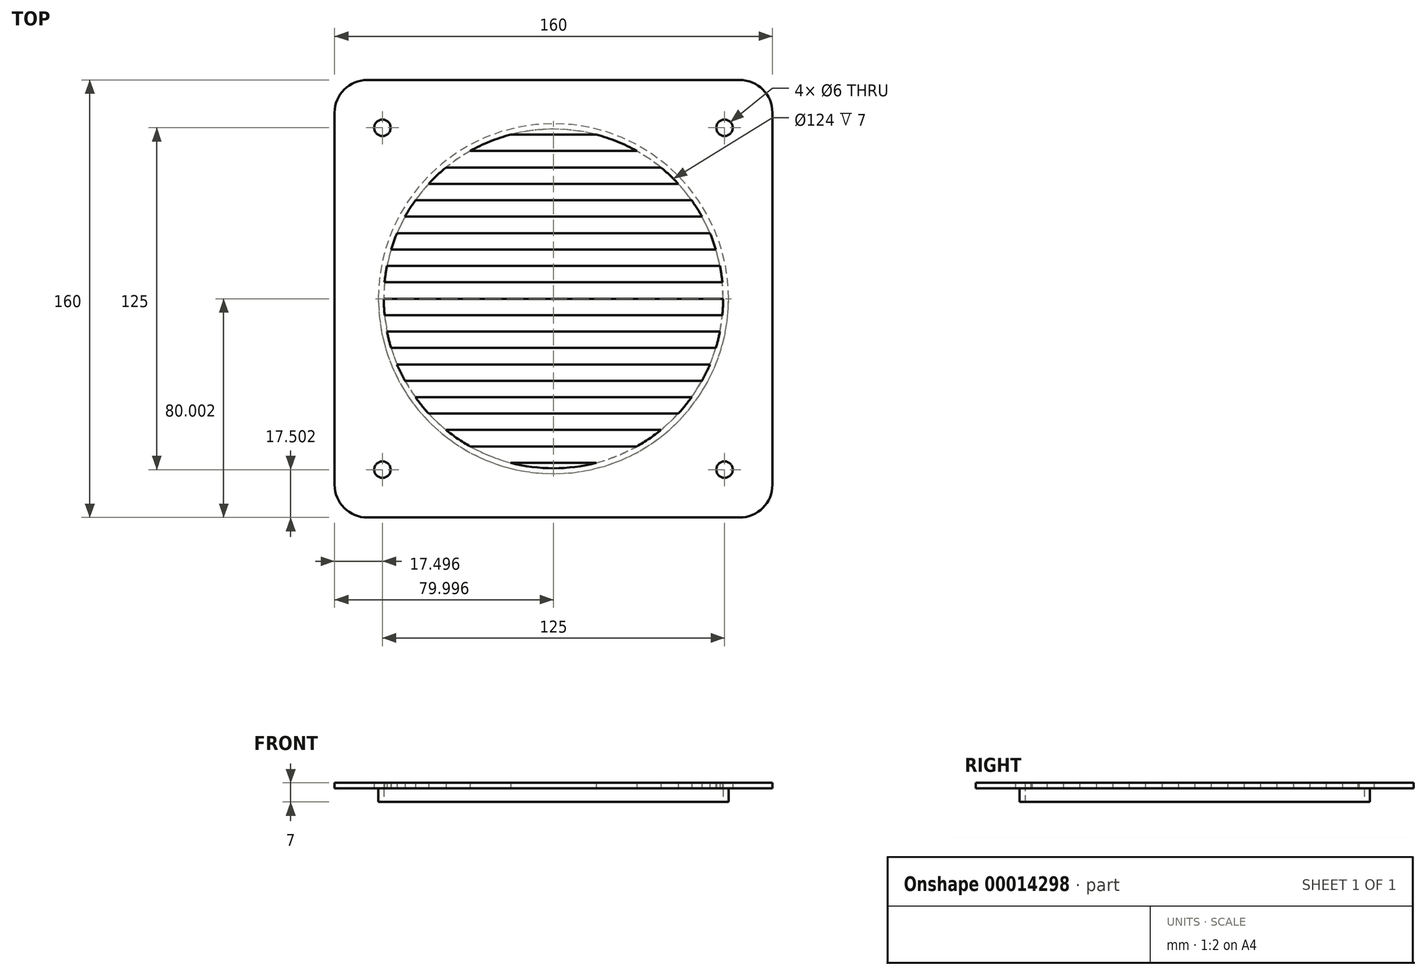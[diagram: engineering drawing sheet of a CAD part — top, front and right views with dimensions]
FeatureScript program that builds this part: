
annotation { "Feature Type Name" : "Feature", "Feature Type Description" : "" }
export const myFeature = defineFeature(function(context is Context, id is Id, definition is map)
    precondition{}
    {
        {
            var Q0;
            Q0=qCreatedBy(makeId("Top.planeOp"),FACE);
            var sketch = newSketch(context, id + "F0", { "sketchPlane" : qUnion([Q0])});
            skLineSegment(sketch, "E0.bottom", {"start": v(-104.32, 77.03) * mm, "end": v(55.68, 77.03) * mm});
            skLineSegment(sketch, "E0.top", {"start": v(-104.32, -82.97) * mm, "end": v(55.68, -82.97) * mm});
            skLineSegment(sketch, "E0.left", {"start": v(-104.32, 77.03) * mm, "end": v(-104.32, -82.97) * mm});
            skLineSegment(sketch, "E0.right", {"start": v(55.68, 77.03) * mm, "end": v(55.68, -82.97) * mm});
            skLineSegment(sketch, "E1", {"start": v(-24.32, 77.03) * mm, "end": v(-24.32, -82.97) * mm, "construction": true});
            skLineSegment(sketch, "E2", {"start": v(-104.32, -2.97) * mm, "end": v(55.68, -2.97) * mm, "construction": true});
            skPoint(sketch, "E3", {"position": v(-24.32, -2.97) * mm});
            skCircle(sketch, "E4", {"center": v(-24.32, -2.97) * mm, "radius": 62 * mm});
            skLineSegment(sketch, "E5", {"start": v(-86.32, -2.97) * mm, "end": v(37.68, -2.97) * mm});
            skLineSegment(sketch, "E6", {"start": v(-86.03, 3.03) * mm, "end": v(37.38, 3.03) * mm});
            skLineSegment(sketch, "E7", {"start": v(-85.15, 9.03) * mm, "end": v(36.5, 9.03) * mm});
            skLineSegment(sketch, "E8", {"start": v(-83.65, 15.03) * mm, "end": v(35, 15.03) * mm});
            skLineSegment(sketch, "E9", {"start": v(-81.5, 21.03) * mm, "end": v(32.84, 21.03) * mm});
            skLineSegment(sketch, "E10", {"start": v(-78.58, 27.03) * mm, "end": v(29.93, 27.03) * mm});
            skLineSegment(sketch, "E11", {"start": v(-74.8, 33.03) * mm, "end": v(26.15, 33.03) * mm});
            skLineSegment(sketch, "E12", {"start": v(-69.93, 39.03) * mm, "end": v(21.28, 39.03) * mm});
            skCircle(sketch, "E13", {"center": v(-86.82, -65.47) * mm, "radius": 3 * mm});
            skLineSegment(sketch, "E14", {"start": v(-86.82, -65.47) * mm, "end": v(-86.82, 59.53) * mm, "construction": true});
            skLineSegment(sketch, "E15", {"start": v(-86.82, 59.53) * mm, "end": v(38.18, 59.53) * mm, "construction": true});
            skLineSegment(sketch, "E16", {"start": v(38.18, 59.53) * mm, "end": v(38.18, -65.47) * mm, "construction": true});
            skLineSegment(sketch, "E17", {"start": v(38.18, -65.47) * mm, "end": v(-86.82, -65.47) * mm, "construction": true});
            skPoint(sketch, "E18", {"position": v(-24.32, 59.53) * mm});
            skPoint(sketch, "E19", {"position": v(38.18, -2.97) * mm});
            skLineSegment(sketch, "E20", {"start": v(-63.57, 45.03) * mm, "end": v(14.92, 45.03) * mm});
            skLineSegment(sketch, "E21", {"start": v(-54.79, 51.03) * mm, "end": v(6.14, 51.03) * mm});
            skLineSegment(sketch, "E22", {"start": v(-39.94, 57.03) * mm, "end": v(-8.7, 57.03) * mm});
            skLineSegment(sketch, "E23.0.MirrorCS", {"start": v(-86.03, -8.97) * mm, "end": v(37.38, -8.97) * mm});
            skLineSegment(sketch, "E23.1.MirrorCS", {"start": v(-85.15, -14.97) * mm, "end": v(36.5, -14.97) * mm});
            skLineSegment(sketch, "E23.2.MirrorCS", {"start": v(-83.65, -20.97) * mm, "end": v(35, -20.97) * mm});
            skLineSegment(sketch, "E23.3.MirrorCS", {"start": v(-81.5, -26.97) * mm, "end": v(32.84, -26.97) * mm});
            skLineSegment(sketch, "E23.4.MirrorCS", {"start": v(-78.58, -32.97) * mm, "end": v(29.93, -32.97) * mm});
            skLineSegment(sketch, "E23.5.MirrorCS", {"start": v(-74.8, -38.97) * mm, "end": v(26.15, -38.97) * mm});
            skLineSegment(sketch, "E23.6.MirrorCS", {"start": v(-69.93, -44.97) * mm, "end": v(21.28, -44.97) * mm});
            skLineSegment(sketch, "E23.7.MirrorCS", {"start": v(-63.57, -50.97) * mm, "end": v(14.92, -50.97) * mm});
            skLineSegment(sketch, "E23.8.MirrorCS", {"start": v(-39.94, -62.97) * mm, "end": v(-8.7, -62.97) * mm});
            skLineSegment(sketch, "E23.9.MirrorCS", {"start": v(-54.79, -56.97) * mm, "end": v(6.14, -56.97) * mm});
            skCircle(sketch, "E24", {"center": v(-86.82, 59.53) * mm, "radius": 3 * mm});
            skCircle(sketch, "E25", {"center": v(38.18, 59.53) * mm, "radius": 3 * mm});
            skCircle(sketch, "E26", {"center": v(38.18, -65.47) * mm, "radius": 3 * mm});
            skSolve(sketch);
        }
        {
            var Q0;
            {var subQ0=sQuery(id+"F0.wireOp",EDGE,"E22");Q0=makeQuery(id+"F0.imprint","IMPRINT",FACE,{"disambiguationData":[TD([[makeQuery(id+"F0.imprint","IMPRINT",EDGE,{"derivedFrom":subQ0}),1.0]])]});}
            var Q1;
            {var subQ1=sQuery(id+"F0.wireOp",EDGE,"E20");Q1=makeQuery(id+"F0.imprint","IMPRINT",FACE,{"disambiguationData":[TD([[makeQuery(id+"F0.imprint","IMPRINT",EDGE,{"derivedFrom":subQ1}),1.0]])]});}
            var Q2;
            {var subQ1=sQuery(id+"F0.wireOp",EDGE,"E11");Q2=makeQuery(id+"F0.imprint","IMPRINT",FACE,{"disambiguationData":[TD([[makeQuery(id+"F0.imprint","IMPRINT",EDGE,{"derivedFrom":subQ1}),1.0]])]});}
            var Q3;
            {var subQ1=sQuery(id+"F0.wireOp",EDGE,"E9");Q3=makeQuery(id+"F0.imprint","IMPRINT",FACE,{"disambiguationData":[TD([[makeQuery(id+"F0.imprint","IMPRINT",EDGE,{"derivedFrom":subQ1}),1.0]])]});}
            var Q4;
            {var subQ1=sQuery(id+"F0.wireOp",EDGE,"E7");Q4=makeQuery(id+"F0.imprint","IMPRINT",FACE,{"disambiguationData":[TD([[makeQuery(id+"F0.imprint","IMPRINT",EDGE,{"derivedFrom":subQ1}),1.0]])]});}
            var Q5;
            {var subQ1=sQuery(id+"F0.wireOp",EDGE,"E5");Q5=makeQuery(id+"F0.imprint","IMPRINT",FACE,{"disambiguationData":[TD([[makeQuery(id+"F0.imprint","IMPRINT",EDGE,{"derivedFrom":subQ1}),1.0]])]});}
            var Q6;
            {var subQ1=sQuery(id+"F0.wireOp",EDGE,"E23.0.MirrorCS");Q6=makeQuery(id+"F0.imprint","IMPRINT",FACE,{"disambiguationData":[TD([[makeQuery(id+"F0.imprint","IMPRINT",EDGE,{"derivedFrom":subQ1}),-1.0]])]});}
            var Q7;
            {var subQ1=sQuery(id+"F0.wireOp",EDGE,"E23.2.MirrorCS");Q7=makeQuery(id+"F0.imprint","IMPRINT",FACE,{"disambiguationData":[TD([[makeQuery(id+"F0.imprint","IMPRINT",EDGE,{"derivedFrom":subQ1}),-1.0]])]});}
            var Q8;
            {var subQ1=sQuery(id+"F0.wireOp",EDGE,"E23.4.MirrorCS");Q8=makeQuery(id+"F0.imprint","IMPRINT",FACE,{"disambiguationData":[TD([[makeQuery(id+"F0.imprint","IMPRINT",EDGE,{"derivedFrom":subQ1}),-1.0]])]});}
            var Q9;
            {var subQ1=sQuery(id+"F0.wireOp",EDGE,"E23.6.MirrorCS");Q9=makeQuery(id+"F0.imprint","IMPRINT",FACE,{"disambiguationData":[TD([[makeQuery(id+"F0.imprint","IMPRINT",EDGE,{"derivedFrom":subQ1}),-1.0]])]});}
            var Q10;
            {var subQ1=sQuery(id+"F0.wireOp",EDGE,"E23.9.MirrorCS");Q10=makeQuery(id+"F0.imprint","IMPRINT",FACE,{"disambiguationData":[TD([[makeQuery(id+"F0.imprint","IMPRINT",EDGE,{"derivedFrom":subQ1}),-1.0]])]});}
            var Q11;
            Q11=makeQuery(id+"F0.imprint","IMPRINT",FACE,{"disambiguationData":[TD([[makeQuery(id+"F0.imprint","IMPRINT",EDGE,{"derivedFrom":sQuery(id+"F0.wireOp",EDGE,"E0.bottom")}),-1.0]])]});
            extrude(context, id + "F1", {"entities" : qUnion([Q0, Q1, Q2, Q3, Q4, Q5, Q6, Q7, Q8, Q9, Q10, Q11]), "depth" : 2 * mm});
        }
        {
            var Q0;
            Q0=makeQuery(id+"F1.opExtrude","SWEPT_EDGE",EDGE,{"disambiguationData":[OSD([sQuery(id+"F0.wireOp",EDGE,"E0.bottom"),sQuery(id+"F0.wireOp",EDGE,"E0.left")])]});
            var Q1;
            Q1=makeQuery(id+"F1.opExtrude","SWEPT_EDGE",EDGE,{"disambiguationData":[OSD([sQuery(id+"F0.wireOp",EDGE,"E0.bottom"),sQuery(id+"F0.wireOp",EDGE,"E0.right")])]});
            var Q2;
            Q2=makeQuery(id+"F1.opExtrude","SWEPT_EDGE",EDGE,{"disambiguationData":[OSD([sQuery(id+"F0.wireOp",EDGE,"E0.top"),sQuery(id+"F0.wireOp",EDGE,"E0.right")])]});
            var Q3;
            Q3=makeQuery(id+"F1.opExtrude","SWEPT_EDGE",EDGE,{"disambiguationData":[OSD([sQuery(id+"F0.wireOp",EDGE,"E0.top"),sQuery(id+"F0.wireOp",EDGE,"E0.left")])]});
            fillet(context, id + "F2", {"entities" : qUnion([Q0, Q1, Q2, Q3]), "radius" : 12 * mm, "tangentPropagation" : true, "allowEdgeOverflow" : false});
        }
        {
            var Q0;
            Q0=makeQuery(id+"F1.opExtrude","CAP_FACE",FACE,{"disambiguationData":[OSD([sQuery(id+"F0.wireOp",EDGE,"E0.bottom"),sQuery(id+"F0.wireOp",EDGE,"E0.top"),sQuery(id+"F0.wireOp",EDGE,"E0.left"),sQuery(id+"F0.wireOp",EDGE,"E0.right"),sQuery(id+"F0.wireOp",EDGE,"E4"),sQuery(id+"F0.wireOp",EDGE,"E5"),sQuery(id+"F0.wireOp",EDGE,"E6"),sQuery(id+"F0.wireOp",EDGE,"E7"),sQuery(id+"F0.wireOp",EDGE,"E8"),sQuery(id+"F0.wireOp",EDGE,"E9"),sQuery(id+"F0.wireOp",EDGE,"E10"),sQuery(id+"F0.wireOp",EDGE,"E11"),sQuery(id+"F0.wireOp",EDGE,"E12"),sQuery(id+"F0.wireOp",EDGE,"E13"),sQuery(id+"F0.wireOp",EDGE,"E20"),sQuery(id+"F0.wireOp",EDGE,"E21"),sQuery(id+"F0.wireOp",EDGE,"E22"),sQuery(id+"F0.wireOp",EDGE,"E23.0.MirrorCS"),sQuery(id+"F0.wireOp",EDGE,"E23.1.MirrorCS"),sQuery(id+"F0.wireOp",EDGE,"E23.2.MirrorCS"),sQuery(id+"F0.wireOp",EDGE,"E23.3.MirrorCS"),sQuery(id+"F0.wireOp",EDGE,"E23.4.MirrorCS"),sQuery(id+"F0.wireOp",EDGE,"E23.5.MirrorCS"),sQuery(id+"F0.wireOp",EDGE,"E23.6.MirrorCS"),sQuery(id+"F0.wireOp",EDGE,"E23.7.MirrorCS"),sQuery(id+"F0.wireOp",EDGE,"E23.9.MirrorCS"),sQuery(id+"F0.wireOp",EDGE,"E23.8.MirrorCS")])],"isStart":true});
            var sketch = newSketch(context, id + "F3", { "sketchPlane" : qUnion([Q0])});
            skLineSegment(sketch, "E27", {"start": v(-24.32, -77.03) * mm, "end": v(-24.32, 82.97) * mm, "construction": true});
            skLineSegment(sketch, "E28", {"start": v(55.68, 2.97) * mm, "end": v(-104.32, 2.97) * mm, "construction": true});
            skPoint(sketch, "E29", {"position": v(-24.32, 2.97) * mm});
            skCircle(sketch, "E30", {"center": v(-24.32, 2.97) * mm, "radius": 62 * mm});
            skCircle(sketch, "E31", {"center": v(-24.32, 2.97) * mm, "radius": 64 * mm});
            skSolve(sketch);
        }
        {
            var Q0;
            Q0=makeQuery(id+"F3.imprint","IMPRINT",FACE,{"disambiguationData":[TD([[makeQuery(id+"F3.imprint","IMPRINT",EDGE,{"derivedFrom":sQuery(id+"F3.wireOp",EDGE,"E31")}),1.0]])]});
            extrude(context, id + "F4", {"entities" : qUnion([Q0]), "operationType" : NewBodyOperationType.ADD, "depth" : 5 * mm});
        }
    });
